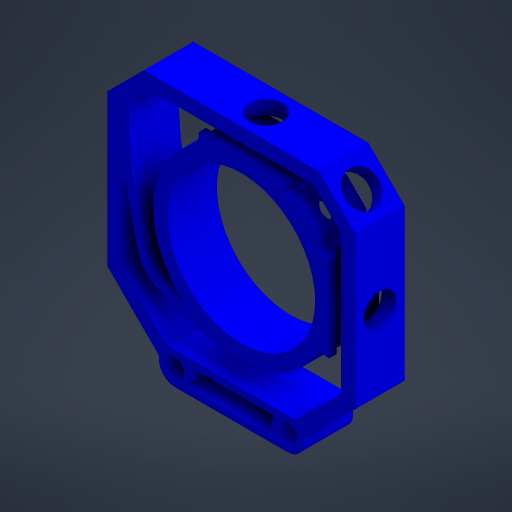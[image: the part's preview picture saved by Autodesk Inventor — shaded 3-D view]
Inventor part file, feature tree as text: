
AUTODESK INVENTOR PART (.ipt)
format: ipt  version: 2023.4 (Build 274418000, 418)  size: 426,496 bytes
history: native  units: mm
features: extrude x6, projected_geometry x4, reference x4, other x3, plane x1, mirror x1, chamfer x1, sketch x1
ambient origin geometry x8: Origin, YZ Plane, XZ Plane, XY Plane, X Axis, Y Axis, Z Axis, Center Point
bodies: Solid1 (feature_tree)
feature tree (21):
  extrude  "Extrusion1"  TaperAngle=45.0deg  [1 undecoded]
  extrude  "Extrusion2"  Depth=5.0mm
  extrude  "Extrusion3"  Depth=5.0mm
  extrude  "Extrusion4"  Depth=5.0mm
  plane  "Work Plane1"
  mirror  "Mirror1"
  extrude  "Extrusion5"  Depth=5.0mm
  extrude  "Extrusion6"  Depth=5.0mm
  chamfer  "Chamfer1"  Distance=2.0mm
  sketch  "Sketch1"  dims[d2=2.5mm d3=45.0deg d4=26.25mm d5=2.5mm d6=2.5mm d7=1.0mm d8=15.0mm d9=2.0mm d10=0.625mm d11=5.0mm d12=135.0deg d13=3.0mm d14=2.0mm d15=2.0mm d16=38.935534mm d17=38.935534mm d18=9.25mm d19=9.25mm d20=9.25mm d21=9.25mm d22=5.0mm d23=5.0mm d24=5.0mm d25=5.0mm d26=2.5mm d28=8.75mm d29=0.0mm d30=1.875mm d31=1.25mm d32=0.0mm d33=5.75mm d34=10.0mm d35=0.0mm d36=1.25mm d37=135.0deg d38=10.0mm d39=0.0mm d40=3.75mm d41=6.0mm d42=10.0mm d43=0.0mm d44=10.0mm d45=0.0mm d48=17.5mm d49=5.0mm d50=1.25mm d51=2.5mm d52=2.5mm d53=1.075mm d54=2.0mm d55=45.0deg d56=0.1425mm d57=0.1425mm d58=1.25mm d59=1.25mm]
  projected_geometry  "Projected Loop1"
  projected_geometry  "Projected Loop2"
  projected_geometry  "Projected Loop3"
  projected_geometry  "Projected Loop4"
  reference  "Reference4"
  reference  "Reference5"
  reference  "Reference6"
  reference  "Reference7"
  other  "<path>\Projects\Project Protocube\Protocube\CAD, STL, OBJ Files\1 CAD\Cube 1x1 V5.iam"
  other  "Cube 1x1 V5.iam"
  other  "Cube 1x1 Bottom V5 Closed Slotted:1"
note: 1 required parameter value undecoded (feature->parameter linkage not recoverable at this tier; creation-order binding heuristic only, values carry confidence <= 0.55)
note: 1 file-system path scrubbed to <path> (originals preserved in map.json)
